# Revit family: Faucet-Single-DXV-Modulus-D35120152RB
name_source: partatom
category: Plumbing Fixtures
units: mm (PartAtom-declared; Revit-internal decimal feet)

## family parameters
Always vertical = No
Cut with Voids When Loaded = Yes
OmniClass Number = 23.45.55.14
OmniClass Title = Single Faucets
Part Type = Normal
Room Calculation Point = No
Round Connector Dimension = Use Radius
Shared = Yes
Work Plane-Based = Yes

## types (1)
- D35120152RB.100
    ASME A112.18.1/CSA B125.1 = Yes
    Assembly Code = D2020300
    CW Connection = No
    CWFU = 1.5
    Default Elevation = 0"
    Description = DXV Modulus Vessel Faucet
    EPA WaterSense® Certified = Yes
    Finish = Brass-DXV-100-Polished Chrome
    Finish 2 = Brass-DXV-144-Brushed Nickel
    Flow Rate = 1.2 gpm (4.5 L/min)
    HW Connection = No
    HWFU = 1.5
    Height = 10 11/16"
    Installation Type = Deck Mounted
    Length = 6 15/16"
    Manufacturer = DXV
    Material = Brass-DXV-100-Polished Chrome
    Model = D35120152RB.100
    NSF 61/Section 9 = Yes
    Price = Prices may vary. Please consult Manufacturer Rep for most up-to-date price list.
    Product Documentation Link = https://dxv01.blob.core.windows.net
    Product Page URL = https://www.dxv.com
    Revised Date = 04/07/2022
    Tempered Water Connection = Yes
    Tempered Water Connection Diameter = 3/8"
    URL = https://www.dxv.com
    Vent Connection = No
    WFU = 2
    Waste Connection = No
    Width = 2 9/16"

## geometry (parser evidence)
native form markers: Sweep x2
no freeform markers — native parametric forms only
